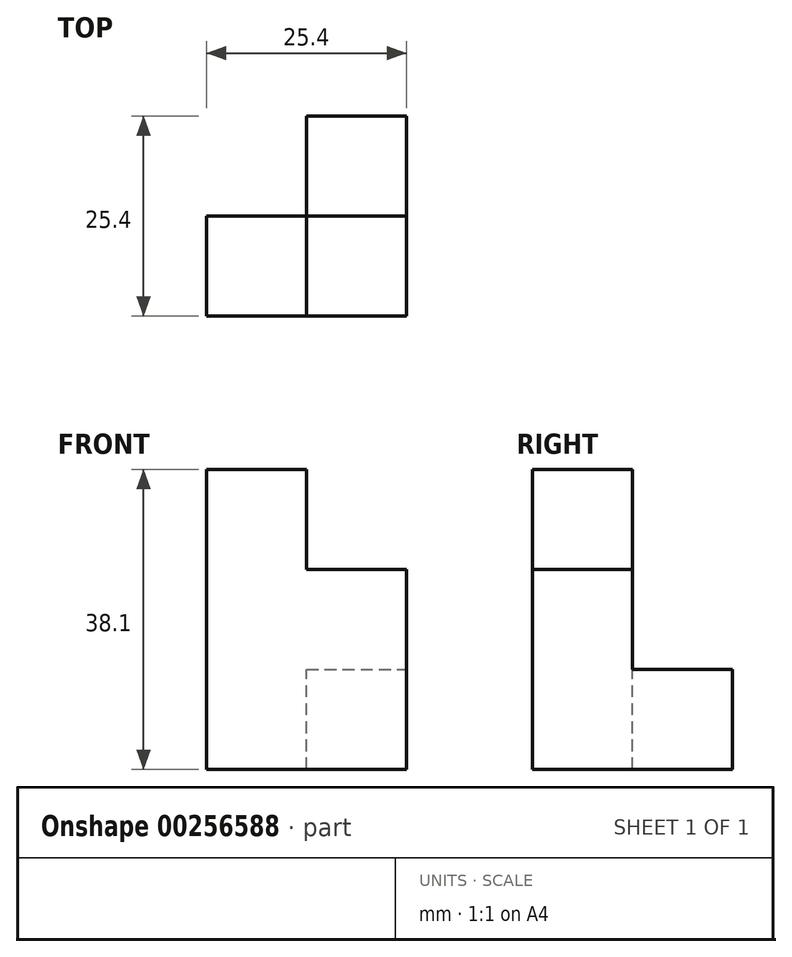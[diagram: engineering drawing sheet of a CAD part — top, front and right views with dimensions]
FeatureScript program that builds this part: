
annotation { "Feature Type Name" : "Feature", "Feature Type Description" : "" }
export const myFeature = defineFeature(function(context is Context, id is Id, definition is map)
    precondition{}
    {
        {
            var Q0;
            Q0=qCreatedBy(makeId("Front.planeOp"),FACE);
            var sketch = newSketch(context, id + "F0", { "sketchPlane" : qUnion([Q0])});
            skLineSegment(sketch, "E0", {"start": v(0, 0) * mm, "end": v(0, 38.1) * mm});
            skLineSegment(sketch, "E1", {"start": v(0, 38.1) * mm, "end": v(12.7, 38.1) * mm});
            skLineSegment(sketch, "E2", {"start": v(12.7, 38.1) * mm, "end": v(12.7, 25.4) * mm});
            skLineSegment(sketch, "E3", {"start": v(12.7, 25.4) * mm, "end": v(25.4, 25.4) * mm});
            skLineSegment(sketch, "E4", {"start": v(25.4, 25.4) * mm, "end": v(25.4, 0) * mm});
            skLineSegment(sketch, "E5", {"start": v(25.4, 0) * mm, "end": v(0, 0) * mm});
            skSolve(sketch);
        }
        {
            var Q0;
            Q0 = qSketchRegion(id + "F0", true);
            extrude(context, id + "F1", {"entities" : qUnion([Q0]), "depth" : 12.7 * mm});
        }
        {
            var Q0;
            Q0=makeQuery(id+"F1.opExtrude","CAP_FACE",FACE,{"disambiguationData":[OSD([sQuery(id+"F0.wireOp",EDGE,"E0"),sQuery(id+"F0.wireOp",EDGE,"E1"),sQuery(id+"F0.wireOp",EDGE,"E2"),sQuery(id+"F0.wireOp",EDGE,"E3"),sQuery(id+"F0.wireOp",EDGE,"E4"),sQuery(id+"F0.wireOp",EDGE,"E5")])],"isStart":true});
            var sketch = newSketch(context, id + "F2", { "sketchPlane" : qUnion([Q0])});
            skLineSegment(sketch, "E6", {"start": v(-25.4, 0) * mm, "end": v(-12.7, 0) * mm});
            skLineSegment(sketch, "E7", {"start": v(-12.7, 0) * mm, "end": v(-12.7, 12.7) * mm});
            skLineSegment(sketch, "E8", {"start": v(-12.7, 12.7) * mm, "end": v(-25.4, 12.7) * mm});
            skLineSegment(sketch, "E9", {"start": v(-25.4, 12.7) * mm, "end": v(-25.4, 0) * mm});
            skSolve(sketch);
        }
        {
            var Q0;
            Q0=makeQuery(id+"F2.imprint","IMPRINT",FACE,{"disambiguationData":[TD([[makeQuery(id+"F2.imprint","IMPRINT",EDGE,{"derivedFrom":sQuery(id+"F2.wireOp",EDGE,"E6")}),1.0]])]});
            extrude(context, id + "F3", {"entities" : qUnion([Q0]), "operationType" : NewBodyOperationType.ADD, "depth" : 12.7 * mm});
        }
    });
